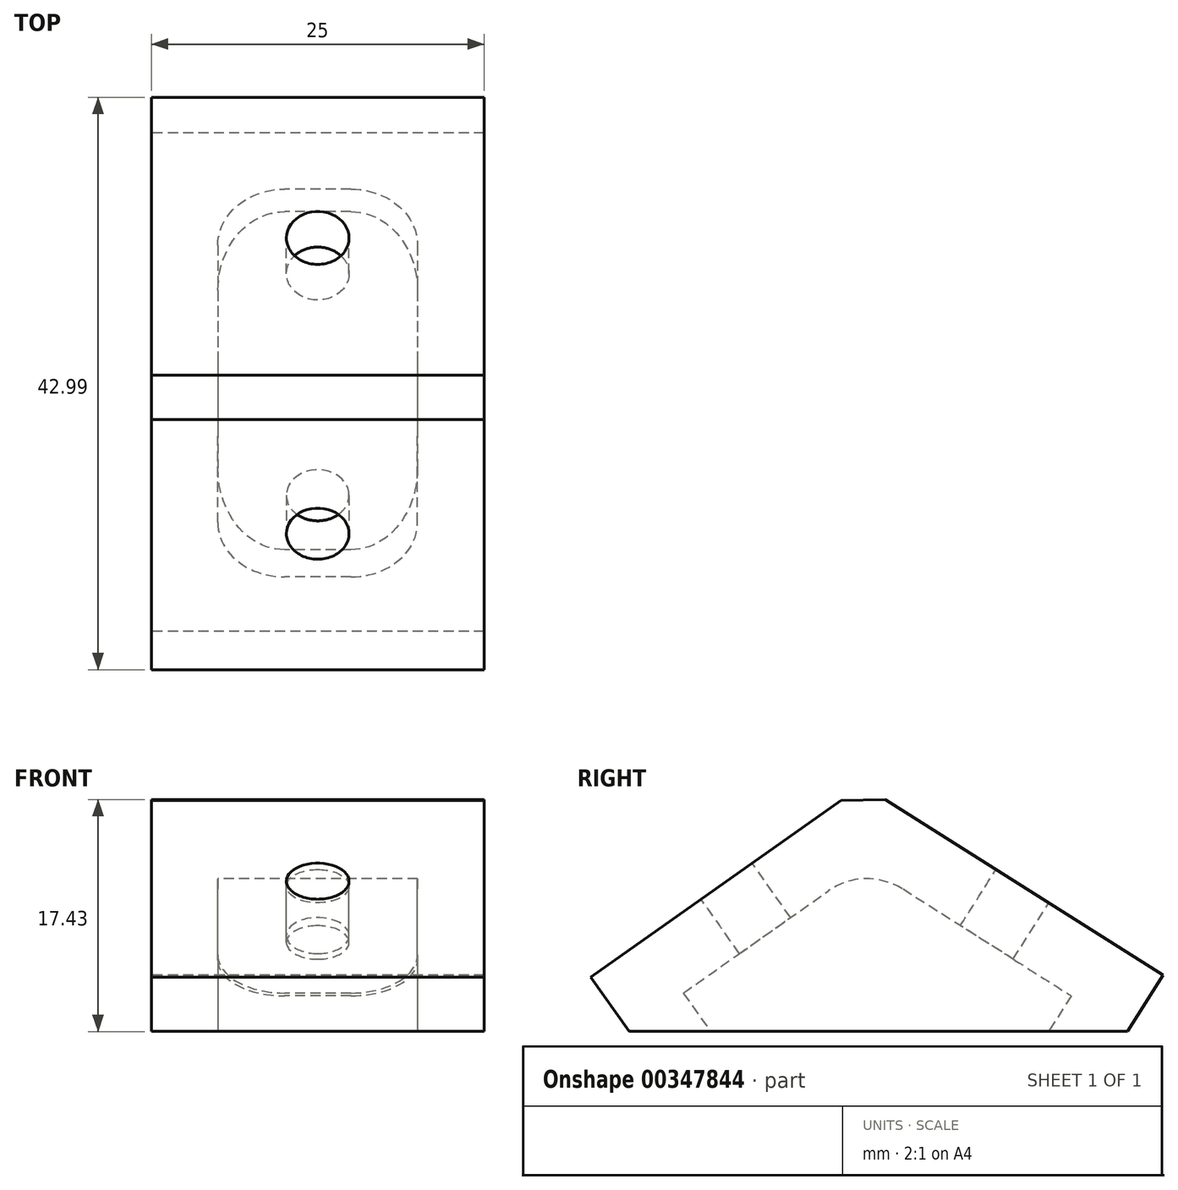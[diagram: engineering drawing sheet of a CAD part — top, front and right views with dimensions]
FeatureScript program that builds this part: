
annotation { "Feature Type Name" : "Feature", "Feature Type Description" : "" }
export const myFeature = defineFeature(function(context is Context, id is Id, definition is map)
    precondition{}
    {
        {
            var Q0;
            Q0=qCreatedBy(makeId("Right.planeOp"),FACE);
            var sketch = newSketch(context, id + "F0", { "sketchPlane" : qUnion([Q0])});
            skLineSegment(sketch, "E0", {"start": v(0, -25) * mm, "end": v(0, 0) * mm});
            skLineSegment(sketch, "E1", {"start": v(24.66, 10.21) * mm, "end": v(0, 0) * mm});
            skLineSegment(sketch, "E2", {"start": v(24.66, 10.21) * mm, "end": v(0, -25) * mm, "construction": true});
            skLineSegment(sketch, "E3.0", {"start": v(26.57, 5.6) * mm, "end": v(5, -3.34) * mm});
            skLineSegment(sketch, "E3.1", {"start": v(5, -25) * mm, "end": v(5, -3.34) * mm});
            skLineSegment(sketch, "E4", {"start": v(0, -25) * mm, "end": v(5, -25) * mm});
            skLineSegment(sketch, "E5", {"start": v(24.66, 10.21) * mm, "end": v(26.57, 5.6) * mm});
            skLineSegment(sketch, "E6", {"start": v(26.57, 5.6) * mm, "end": v(5, -25) * mm});
            skSolve(sketch);
        }
        {
            var Q0;
            Q0 = qSketchRegion(id + "F0", true);
            extrude(context, id + "F1", {"entities" : qUnion([Q0]), "depth" : 25 * mm});
        }
        {
            var Q0;
            Q0=makeQuery(id+"F1.opExtrude","SWEPT_FACE",FACE,{"disambiguationData":[OSD([sQuery(id+"F0.wireOp",EDGE,"E6")])]});
            shell(context, id + "F2", {"entities" : qUnion([Q0]), "thickness" : 5 * mm});
        }
        {
            var Q0;
            {var subQ0=sQuery(id+"F0.wireOp",EDGE,"E5");Q0=makeQuery(id+"F2.opShell","OFFSET_EDGE",EDGE,{"disambiguationData":[OSD([subQ0]),TDD([makeQuery(id+"F1.opExtrude","CAP_EDGE",EDGE,{"disambiguationData":[OSD([subQ0])],"isStart":false})])]});}
            var Q1;
            {var subQ0=sQuery(id+"F0.wireOp",EDGE,"E5");Q1=makeQuery(id+"F2.opShell","OFFSET_EDGE",EDGE,{"disambiguationData":[OSD([subQ0]),TDD([makeQuery(id+"F1.opExtrude","CAP_EDGE",EDGE,{"disambiguationData":[OSD([subQ0])],"isStart":true})])]});}
            var Q2;
            {var subQ0=sQuery(id+"F0.wireOp",EDGE,"E4");Q2=makeQuery(id+"F2.opShell","OFFSET_EDGE",EDGE,{"disambiguationData":[OSD([subQ0]),TDD([makeQuery(id+"F1.opExtrude","CAP_EDGE",EDGE,{"disambiguationData":[OSD([subQ0])],"isStart":false})])]});}
            var Q3;
            {var subQ0=sQuery(id+"F0.wireOp",EDGE,"E4");Q3=makeQuery(id+"F2.opShell","OFFSET_EDGE",EDGE,{"disambiguationData":[OSD([subQ0]),TDD([makeQuery(id+"F1.opExtrude","CAP_EDGE",EDGE,{"disambiguationData":[OSD([subQ0])],"isStart":true})])]});}
            fillet(context, id + "F3", {"entities" : qUnion([Q0, Q1, Q2, Q3]), "radius" : 5 * mm, "tangentPropagation" : true, "allowEdgeOverflow" : false});
        }
        {
            var Q0;
            Q0=makeQuery(id+"F2.opShell","OFFSET_EDGE",EDGE,{"disambiguationData":[OSD([sQuery(id+"F0.wireOp",EDGE,"E0"),sQuery(id+"F0.wireOp",EDGE,"E1")])]});
            fillet(context, id + "F4", {"entities" : qUnion([Q0]), "radius" : 5 * mm, "tangentPropagation" : true, "allowEdgeOverflow" : false});
        }
        {
            var Q0;
            Q0=makeQuery(id+"F1.opExtrude","SWEPT_EDGE",EDGE,{"disambiguationData":[OSD([sQuery(id+"F0.wireOp",EDGE,"E0"),sQuery(id+"F0.wireOp",EDGE,"E1")])]});
            chamfer(context, id + "F5", {"entities" : qUnion([Q0]), "width" : 3 * mm, "tangentPropagation" : true});
        }
        {
            var Q0;
            Q0=makeQuery(id+"F1.opExtrude","SWEPT_FACE",FACE,{"disambiguationData":[OSD([sQuery(id+"F0.wireOp",EDGE,"E1")])]});
            var sketch = newSketch(context, id + "F6", { "sketchPlane" : qUnion([Q0])});
            skCircle(sketch, "E7", {"center": v(12.5, 14.19) * mm, "radius": 2.35 * mm});
            skLineSegment(sketch, "E8.0", {"start": v(0, 26.69) * mm, "end": v(0, 3) * mm, "construction": true});
            skLineSegment(sketch, "E9.0", {"start": v(0, 3) * mm, "end": v(25, 3) * mm, "construction": true});
            skLineSegment(sketch, "E10.0", {"start": v(25, 26.69) * mm, "end": v(0, 26.69) * mm, "construction": true});
            skLineSegment(sketch, "E11.0", {"start": v(25, 26.69) * mm, "end": v(25, 3) * mm, "construction": true});
            skSolve(sketch);
        }
        {
            var Q0;
            Q0=makeQuery(id+"F6.imprint","IMPRINT",FACE,{"disambiguationData":[TD([[makeQuery(id+"F6.imprint","IMPRINT",EDGE,{"derivedFrom":sQuery(id+"F6.wireOp",EDGE,"E7")}),1.0]])]});
            extrude(context, id + "F7", {"entities" : qUnion([Q0]), "operationType" : NewBodyOperationType.REMOVE, "oppositeDirection" : true, "depth" : 25 * mm});
        }
        {
            var Q0;
            Q0=makeQuery(id+"F1.opExtrude","SWEPT_FACE",FACE,{"disambiguationData":[OSD([sQuery(id+"F0.wireOp",EDGE,"E0")])]});
            var sketch = newSketch(context, id + "F8", { "sketchPlane" : qUnion([Q0])});
            skLineSegment(sketch, "E12.0", {"start": v(0, -25) * mm, "end": v(0, -3) * mm, "construction": true});
            skLineSegment(sketch, "E13.0", {"start": v(25, -25) * mm, "end": v(0, -25) * mm, "construction": true});
            skCircle(sketch, "E14", {"center": v(12.5, -12.5) * mm, "radius": 2.35 * mm});
            skSolve(sketch);
        }
        {
            var Q0;
            Q0 = qSketchRegion(id + "F8", true);
            extrude(context, id + "F9", {"entities" : qUnion([Q0]), "operationType" : NewBodyOperationType.REMOVE, "oppositeDirection" : true, "depth" : 25 * mm});
        }
        {
            var Q0;
            Q0=makeQuery(id+"F1.opExtrude","SWEPT_BODY",BODY,{"disambiguationData":[OSD([sQuery(id+"F0.wireOp",EDGE,"E0"),sQuery(id+"F0.wireOp",EDGE,"E1"),sQuery(id+"F0.wireOp",EDGE,"E4"),sQuery(id+"F0.wireOp",EDGE,"E5"),sQuery(id+"F0.wireOp",EDGE,"E6")])]});
            var Q1;
            Q1=qCreatedBy(makeId("Top.planeOp"),FACE);
            transform(context, id + "F10", {"entities" : qUnion([Q0]), "transformType" : TransformType.TRANSLATION_DISTANCE, "transformDirection" : qUnion([Q1]), "distance" : 19.8 * mm, "makeCopy" : false});
        }
        {
            var Q0;
            Q0=makeQuery(id+"F1.opExtrude","SWEPT_BODY",BODY,{"disambiguationData":[OSD([sQuery(id+"F0.wireOp",EDGE,"E0"),sQuery(id+"F0.wireOp",EDGE,"E1"),sQuery(id+"F0.wireOp",EDGE,"E4"),sQuery(id+"F0.wireOp",EDGE,"E5"),sQuery(id+"F0.wireOp",EDGE,"E6")])]});
            var Q1;
            {var subQ0=sQuery(id+"F0.wireOp",EDGE,"E0");Q1=makeQuery(id+"F5.opChamfer","BLEND_EDGE",EDGE,{"blendedFrom":[makeQuery(id+"F1.opExtrude","SWEPT_EDGE",EDGE,{"disambiguationData":[OSD([subQ0,sQuery(id+"F0.wireOp",EDGE,"E1")])]}),makeQuery(id+"F1.opExtrude","SWEPT_FACE",FACE,{"disambiguationData":[OSD([subQ0])]})],"blendedInto":[makeQuery(id+"F1.opExtrude","SWEPT_FACE",FACE,{"disambiguationData":[OSD([subQ0])]})]});}
            transform(context, id + "F11", {"entities" : qUnion([Q0]), "transformType" : TransformType.ROTATION, "transformAxis" : qUnion([Q1]), "angle" : 54.8 * degree, "makeCopy" : false});
        }
    });
